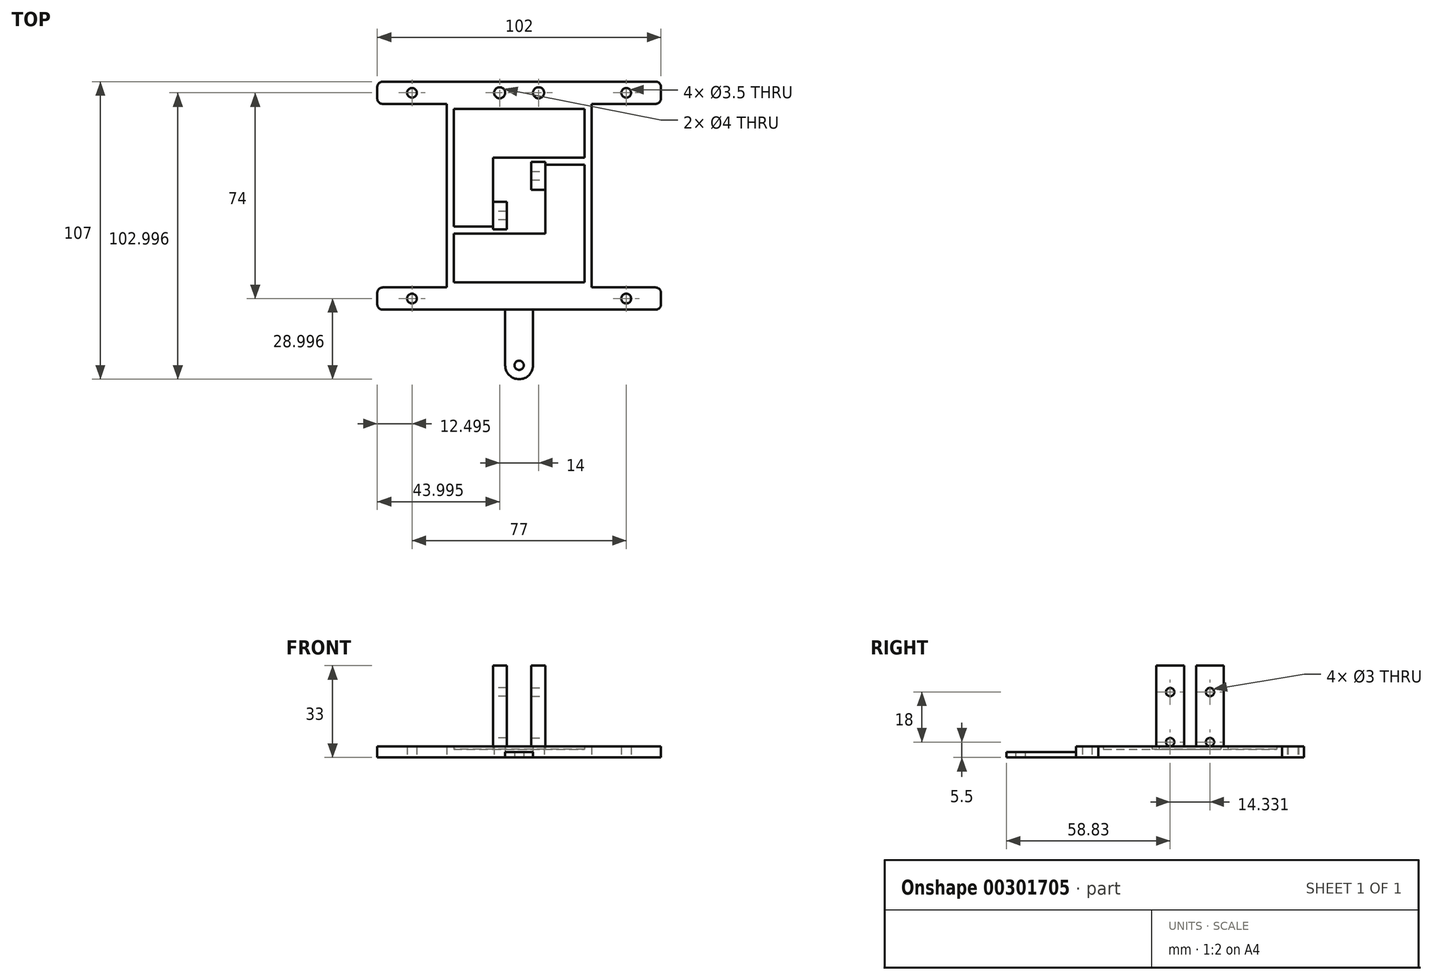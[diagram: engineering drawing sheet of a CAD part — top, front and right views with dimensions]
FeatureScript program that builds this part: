
annotation { "Feature Type Name" : "Feature", "Feature Type Description" : "" }
export const myFeature = defineFeature(function(context is Context, id is Id, definition is map)
    precondition{}
    {
        {
            var Q0;
            Q0=qCreatedBy(makeId("Top.planeOp"),FACE);
            var sketch = newSketch(context, id + "F0", { "sketchPlane" : qUnion([Q0])});
            skPoint(sketch, "E0.middle", {"position": v(0.82, 10.68) * mm});
            skPoint(sketch, "E1.orphan", {"position": v(-52.18, 95.18) * mm});
            skPoint(sketch, "E2.orphan", {"position": v(53.82, 95.18) * mm});
            skPoint(sketch, "E3.orphan", {"position": v(-52.18, 18.18) * mm});
            skLineSegment(sketch, "E4", {"start": v(24.32, 67.78) * mm, "end": v(10.22, 67.78) * mm});
            skLineSegment(sketch, "E5", {"start": v(10.22, 67.78) * mm, "end": v(10.22, 42.98) * mm});
            skLineSegment(sketch, "E6", {"start": v(10.22, 42.98) * mm, "end": v(-22.68, 42.98) * mm});
            skPoint(sketch, "E7.end.orphan", {"position": v(16.44, 67.78) * mm});
            skLineSegment(sketch, "E8", {"start": v(-22.68, 45.48) * mm, "end": v(-8.58, 45.48) * mm});
            skLineSegment(sketch, "E9", {"start": v(-8.58, 45.48) * mm, "end": v(-8.58, 70.28) * mm});
            skLineSegment(sketch, "E10", {"start": v(-8.58, 70.28) * mm, "end": v(24.32, 70.28) * mm});
            skPoint(sketch, "E11.orphan", {"position": v(24.82, 56.68) * mm});
            skPoint(sketch, "E12.start.orphan", {"position": v(-17.96, 45.78) * mm});
            skPoint(sketch, "E13.orphan", {"position": v(-44.18, 8.18) * mm});
            skPoint(sketch, "E14.orphan", {"position": v(45.82, 8.18) * mm});
            skLineSegment(sketch, "E15", {"start": v(-22.68, 45.48) * mm, "end": v(-22.68, 87.78) * mm});
            skPoint(sketch, "E16.orphan", {"position": v(24.82, 67.78) * mm});
            skPoint(sketch, "E17", {"position": v(0.82, 112.58) * mm});
            skPoint(sketch, "E18.end.orphan", {"position": v(51.26, 95.18) * mm});
            skPoint(sketch, "E19.end.orphan", {"position": v(0.87, 21.1) * mm});
            skPoint(sketch, "E0.right.end.orphan", {"position": v(-52.18, -73.82) * mm});
            skPoint(sketch, "E0.left.end.orphan", {"position": v(53.82, -73.82) * mm});
            skPoint(sketch, "E20.bottom.end.orphan", {"position": v(-10.23, 11.86) * mm});
            skPoint(sketch, "E20.bottom.start.orphan", {"position": v(-5, 3.24) * mm});
            skLineSegment(sketch, "E21.top", {"start": v(-8.58, 54.46) * mm, "end": v(-3.58, 54.46) * mm});
            skLineSegment(sketch, "E21.left", {"start": v(-8.58, 44.46) * mm, "end": v(-8.58, 54.46) * mm});
            skLineSegment(sketch, "E21.right", {"start": v(-3.58, 44.46) * mm, "end": v(-3.58, 54.46) * mm});
            skPoint(sketch, "E22.oppositeSnap0", {"position": v(7.87, 70.28) * mm});
            skLineSegment(sketch, "E22.left", {"start": v(10.22, 70.28) * mm, "end": v(10.22, 61.41) * mm});
            skPoint(sketch, "E23.end.orphan", {"position": v(7.87, 63.28) * mm});
            skLineSegment(sketch, "E24.bottom", {"start": v(10.22, 70.28) * mm, "end": v(7.22, 70.28) * mm});
            skLineSegment(sketch, "E24.top", {"start": v(10.22, 58.8) * mm, "end": v(5.22, 58.8) * mm});
            skLineSegment(sketch, "E24.left", {"start": v(10.22, 68.8) * mm, "end": v(10.22, 58.8) * mm});
            skLineSegment(sketch, "E24.right", {"start": v(5.22, 68.8) * mm, "end": v(5.22, 58.8) * mm});
            skLineSegment(sketch, "E25", {"start": v(-22.68, 25.48) * mm, "end": v(-22.68, 42.98) * mm});
            skLineSegment(sketch, "E26", {"start": v(24.32, 87.78) * mm, "end": v(24.32, 70.28) * mm});
            skLineSegment(sketch, "E27", {"start": v(-22.68, 87.78) * mm, "end": v(24.32, 87.78) * mm});
            skLineSegment(sketch, "E28", {"start": v(-22.68, 25.48) * mm, "end": v(24.32, 25.48) * mm});
            skPoint(sketch, "E29.end.orphan", {"position": v(24.32, 26.57) * mm});
            skLineSegment(sketch, "E30", {"start": v(24.32, 25.48) * mm, "end": v(24.32, 67.78) * mm});
            skLineSegment(sketch, "E31", {"start": v(-8.58, 44.46) * mm, "end": v(-3.58, 44.46) * mm});
            skLineSegment(sketch, "E32", {"start": v(5.22, 68.8) * mm, "end": v(10.22, 68.8) * mm});
            skLineSegment(sketch, "E33.bottom", {"start": v(-25.18, 97.63) * mm, "end": v(26.82, 97.63) * mm});
            skLineSegment(sketch, "E33.top", {"start": v(-25.18, 15.63) * mm, "end": v(26.82, 15.63) * mm});
            skLineSegment(sketch, "E33.left", {"start": v(-25.18, 89.63) * mm, "end": v(-25.18, 23.63) * mm});
            skLineSegment(sketch, "E33.right", {"start": v(26.82, 89.63) * mm, "end": v(26.82, 23.63) * mm});
            skLineSegment(sketch, "E34.bottom", {"start": v(26.82, 97.63) * mm, "end": v(51.82, 97.63) * mm});
            skLineSegment(sketch, "E34.top", {"start": v(26.82, 89.63) * mm, "end": v(51.82, 89.63) * mm});
            skLineSegment(sketch, "E34.right", {"start": v(51.82, 97.63) * mm, "end": v(51.82, 89.63) * mm});
            skLineSegment(sketch, "E35.bottom", {"start": v(-25.18, 97.63) * mm, "end": v(-50.18, 97.63) * mm});
            skLineSegment(sketch, "E35.top", {"start": v(-25.18, 89.63) * mm, "end": v(-50.18, 89.63) * mm});
            skLineSegment(sketch, "E35.right", {"start": v(-50.18, 97.63) * mm, "end": v(-50.18, 89.63) * mm});
            skLineSegment(sketch, "E36.bottom", {"start": v(-25.18, 15.63) * mm, "end": v(-50.18, 15.63) * mm});
            skLineSegment(sketch, "E36.top", {"start": v(-25.18, 23.63) * mm, "end": v(-50.18, 23.63) * mm});
            skLineSegment(sketch, "E36.right", {"start": v(-50.18, 15.63) * mm, "end": v(-50.18, 23.63) * mm});
            skLineSegment(sketch, "E37.bottom", {"start": v(26.82, 15.63) * mm, "end": v(51.82, 15.63) * mm});
            skLineSegment(sketch, "E37.top", {"start": v(26.82, 23.63) * mm, "end": v(51.82, 23.63) * mm});
            skLineSegment(sketch, "E37.right", {"start": v(51.82, 15.63) * mm, "end": v(51.82, 23.63) * mm});
            skLineSegment(sketch, "E38", {"start": v(-25.18, 15.63) * mm, "end": v(-50.18, 23.63) * mm, "construction": true});
            skLineSegment(sketch, "E39", {"start": v(-50.18, 15.63) * mm, "end": v(-25.18, 23.63) * mm, "construction": true});
            skCircle(sketch, "E40", {"center": v(-37.68, 19.63) * mm, "radius": 1.75 * mm});
            skLineSegment(sketch, "E41", {"start": v(51.82, 15.63) * mm, "end": v(26.82, 23.63) * mm, "construction": true});
            skLineSegment(sketch, "E42", {"start": v(26.82, 15.63) * mm, "end": v(51.82, 23.63) * mm, "construction": true});
            skCircle(sketch, "E43", {"center": v(39.32, 19.63) * mm, "radius": 1.75 * mm});
            skLineSegment(sketch, "E44", {"start": v(51.82, 89.63) * mm, "end": v(26.82, 97.63) * mm, "construction": true});
            skLineSegment(sketch, "E45", {"start": v(26.82, 89.63) * mm, "end": v(51.82, 97.63) * mm, "construction": true});
            skCircle(sketch, "E46", {"center": v(39.32, 93.63) * mm, "radius": 1.75 * mm});
            skLineSegment(sketch, "E47", {"start": v(-25.18, 89.63) * mm, "end": v(-50.18, 97.63) * mm, "construction": true});
            skLineSegment(sketch, "E48", {"start": v(-50.18, 89.63) * mm, "end": v(-25.18, 97.63) * mm, "construction": true});
            skCircle(sketch, "E49", {"center": v(-37.68, 93.63) * mm, "radius": 1.75 * mm});
            skLineSegment(sketch, "E50.left", {"start": v(5.82, -4.37) * mm, "end": v(5.82, 15.63) * mm});
            skLineSegment(sketch, "E50.right", {"start": v(-4.18, -4.37) * mm, "end": v(-4.18, 15.63) * mm});
            skCircle(sketch, "E51", {"center": v(0.82, -4.37) * mm, "radius": 1.67 * mm});
            skArc(sketch, "E52", {"start": v(-4.18, -4.37) * mm, "mid": v(0.82, -9.37) * mm, "end": v(5.82, -4.37) * mm});
            skLineSegment(sketch, "E53", {"start": v(-4.18, -4.37) * mm, "end": v(5.82, -4.37) * mm, "construction": true});
            skLineSegment(sketch, "E54", {"start": v(-37.68, 93.63) * mm, "end": v(39.32, 93.63) * mm, "construction": true});
            skCircle(sketch, "E55", {"center": v(-6.18, 93.63) * mm, "radius": 2 * mm});
            skCircle(sketch, "E56", {"center": v(7.82, 93.63) * mm, "radius": 2 * mm});
            skSolve(sketch);
        }
        {
            var Q0;
            {var subQ2=sQuery(id+"F0.wireOp",EDGE,"E4");Q0=makeQuery(id+"F0.imprint","IMPRINT",FACE,{"disambiguationData":[TD([[makeQuery(id+"F0.imprint","IMPRINT",EDGE,{"derivedFrom":subQ2}),-1.0]])]});}
            extrude(context, id + "F1", {"entities" : qUnion([Q0]), "depth" : 4 * mm, "offsetDistance" : 25 * mm});
        }
        {
            var Q0;
            {var subQ2=sQuery(id+"F0.wireOp",EDGE,"E4");Q0=makeQuery(id+"F0.imprint","IMPRINT",FACE,{"disambiguationData":[TD([[makeQuery(id+"F0.imprint","IMPRINT",EDGE,{"derivedFrom":subQ2}),1.0]])]});}
            var Q1;
            {var subQ4=sQuery(id+"F0.wireOp",EDGE,"E8");Q1=makeQuery(id+"F0.imprint","IMPRINT",FACE,{"disambiguationData":[TD([[makeQuery(id+"F0.imprint","IMPRINT",EDGE,{"derivedFrom":subQ4}),1.0]])]});}
            extrude(context, id + "F2", {"entities" : qUnion([Q0, Q1]), "operationType" : NewBodyOperationType.ADD, "depth" : 3 * mm, "offsetDistance" : 25 * mm});
        }
        {
            var Q0;
            {var subQ0=sQuery(id+"F0.wireOp",EDGE,"E50.left");Q0=makeQuery(id+"F0.imprint","IMPRINT",FACE,{"disambiguationData":[TD([[makeQuery(id+"F0.imprint","IMPRINT",EDGE,{"derivedFrom":subQ0}),1.0]])]});}
            extrude(context, id + "F3", {"entities" : qUnion([Q0]), "operationType" : NewBodyOperationType.ADD, "depth" : 1.9 * mm, "offsetDistance" : 25 * mm});
        }
        {
            var Q0;
            {var subQ1=sQuery(id+"F0.wireOp",EDGE,"E24.top");Q0=makeQuery(id+"F0.imprint","IMPRINT",FACE,{"disambiguationData":[TD([[makeQuery(id+"F0.imprint","IMPRINT",EDGE,{"derivedFrom":subQ1}),-1.0]])]});}
            var Q1;
            {var subQ2=sQuery(id+"F0.wireOp",EDGE,"E21.top");Q1=makeQuery(id+"F0.imprint","IMPRINT",FACE,{"disambiguationData":[TD([[makeQuery(id+"F0.imprint","IMPRINT",EDGE,{"derivedFrom":subQ2}),-1.0]])]});}
            extrude(context, id + "F4", {"entities" : qUnion([Q0, Q1]), "operationType" : NewBodyOperationType.ADD, "depth" : 33 * mm, "offsetDistance" : 25 * mm});
        }
        {
            var Q0;
            Q0=makeQuery(id+"F1.opExtrude","SWEPT_EDGE",EDGE,{"disambiguationData":[OSD([sQuery(id+"F0.wireOp",EDGE,"E34.bottom"),sQuery(id+"F0.wireOp",EDGE,"E34.right")])]});
            var Q1;
            Q1=makeQuery(id+"F1.opExtrude","SWEPT_EDGE",EDGE,{"disambiguationData":[OSD([sQuery(id+"F0.wireOp",EDGE,"E35.bottom"),sQuery(id+"F0.wireOp",EDGE,"E35.right")])]});
            var Q2;
            Q2=makeQuery(id+"F1.opExtrude","SWEPT_EDGE",EDGE,{"disambiguationData":[OSD([sQuery(id+"F0.wireOp",EDGE,"E35.top"),sQuery(id+"F0.wireOp",EDGE,"E35.right")])]});
            var Q3;
            Q3=makeQuery(id+"F1.opExtrude","SWEPT_EDGE",EDGE,{"disambiguationData":[OSD([sQuery(id+"F0.wireOp",EDGE,"E36.bottom"),sQuery(id+"F0.wireOp",EDGE,"E36.right")])]});
            var Q4;
            Q4=makeQuery(id+"F1.opExtrude","SWEPT_EDGE",EDGE,{"disambiguationData":[OSD([sQuery(id+"F0.wireOp",EDGE,"E37.top"),sQuery(id+"F0.wireOp",EDGE,"E37.right")])]});
            var Q5;
            Q5=makeQuery(id+"F1.opExtrude","SWEPT_EDGE",EDGE,{"disambiguationData":[OSD([sQuery(id+"F0.wireOp",EDGE,"E37.bottom"),sQuery(id+"F0.wireOp",EDGE,"E37.right")])]});
            var Q6;
            Q6=makeQuery(id+"F1.opExtrude","SWEPT_EDGE",EDGE,{"disambiguationData":[OSD([sQuery(id+"F0.wireOp",EDGE,"E34.top"),sQuery(id+"F0.wireOp",EDGE,"E34.right")])]});
            var Q7;
            Q7=makeQuery(id+"F1.opExtrude","SWEPT_EDGE",EDGE,{"disambiguationData":[OSD([sQuery(id+"F0.wireOp",EDGE,"E36.top"),sQuery(id+"F0.wireOp",EDGE,"E36.right")])]});
            fillet(context, id + "F5", {"entities" : qUnion([Q0, Q1, Q2, Q3, Q4, Q5, Q6, Q7]), "radius" : 2 * mm, "tangentPropagation" : true, "allowEdgeOverflow" : false});
        }
        {
            var Q0;
            Q0=makeQuery(id+"F4.boolean.opBoolean","MERGE",FACE,{"derivedFrom":[makeQuery(id+"F1.opExtrude","SWEPT_FACE",FACE,{"disambiguationData":[OSD([sQuery(id+"F0.wireOp",EDGE,"E5")])]}),makeQuery(id+"F4.opExtrude","SWEPT_FACE",FACE,{"disambiguationData":[OSD([sQuery(id+"F0.wireOp",EDGE,"E24.left")])]})]});
            cPlane(context, id + "F6", {"entities" : qUnion([Q0]), "cplaneType" : CPlaneType.OFFSET, "offset" : 0 * mm, "width" : 150 * mm, "height" : 150 * mm});
        }
        {
            var Q0;
            Q0=makeQuery(id+"F4.boolean.opBoolean","MERGE",FACE,{"derivedFrom":[makeQuery(id+"F1.opExtrude","SWEPT_FACE",FACE,{"disambiguationData":[OSD([sQuery(id+"F0.wireOp",EDGE,"E9")])]}),makeQuery(id+"F4.opExtrude","SWEPT_FACE",FACE,{"disambiguationData":[OSD([sQuery(id+"F0.wireOp",EDGE,"E21.left")])]})]});
            cPlane(context, id + "F7", {"entities" : qUnion([Q0]), "cplaneType" : CPlaneType.OFFSET, "offset" : 0 * mm, "width" : 150 * mm, "height" : 150 * mm});
        }
        {
            var Q0;
            Q0=qCreatedBy(id+"F6.planeOp",FACE);
            var sketch = newSketch(context, id + "F8", { "sketchPlane" : qUnion([Q0])});
            skCircle(sketch, "E57", {"center": v(63.8, 23.5) * mm, "radius": 1.5 * mm});
            skCircle(sketch, "E58", {"center": v(63.8, 5.5) * mm, "radius": 1.5 * mm});
            skSolve(sketch);
        }
        {
            var Q0;
            Q0=qCreatedBy(id+"F7.planeOp",FACE);
            var sketch = newSketch(context, id + "F9", { "sketchPlane" : qUnion([Q0])});
            skCircle(sketch, "E59", {"center": v(-49.46, 23.5) * mm, "radius": 1.5 * mm});
            skCircle(sketch, "E60", {"center": v(-49.46, 5.5) * mm, "radius": 1.5 * mm});
            skSolve(sketch);
        }
        {
            var Q0;
            Q0=makeQuery(id+"F9.imprint","IMPRINT",FACE,{"disambiguationData":[TD([[makeQuery(id+"F9.imprint","IMPRINT",EDGE,{"derivedFrom":sQuery(id+"F9.wireOp",EDGE,"E59")}),1.0]])]});
            var Q1;
            Q1=makeQuery(id+"F9.imprint","IMPRINT",FACE,{"disambiguationData":[TD([[makeQuery(id+"F9.imprint","IMPRINT",EDGE,{"derivedFrom":sQuery(id+"F9.wireOp",EDGE,"E60")}),1.0]])]});
            extrude(context, id + "F10", {"entities" : qUnion([Q0, Q1]), "operationType" : NewBodyOperationType.REMOVE, "oppositeDirection" : true, "depth" : 25 * mm, "offsetDistance" : 25 * mm});
        }
        {
            var Q0;
            Q0=makeQuery(id+"F8.imprint","IMPRINT",FACE,{"disambiguationData":[TD([[makeQuery(id+"F8.imprint","IMPRINT",EDGE,{"derivedFrom":sQuery(id+"F8.wireOp",EDGE,"E58")}),1.0]])]});
            var Q1;
            Q1=makeQuery(id+"F8.imprint","IMPRINT",FACE,{"disambiguationData":[TD([[makeQuery(id+"F8.imprint","IMPRINT",EDGE,{"derivedFrom":sQuery(id+"F8.wireOp",EDGE,"E57")}),1.0]])]});
            extrude(context, id + "F11", {"entities" : qUnion([Q0, Q1]), "operationType" : NewBodyOperationType.REMOVE, "oppositeDirection" : true, "depth" : 25 * mm, "offsetDistance" : 25 * mm});
        }
    });
